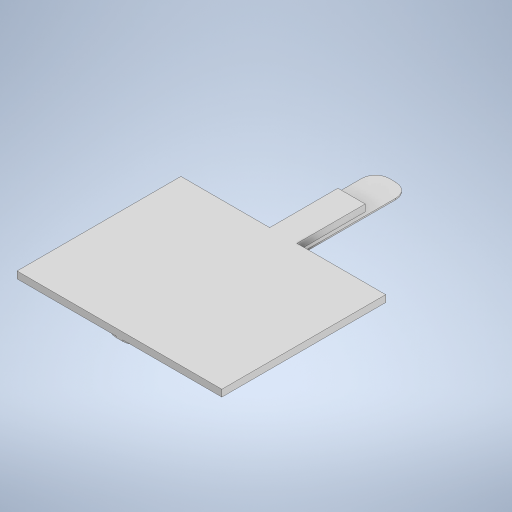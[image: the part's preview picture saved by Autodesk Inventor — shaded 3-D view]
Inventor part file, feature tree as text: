
AUTODESK INVENTOR PART (.ipt)
format: ipt  version: 2023 (Build 270158000, 158)  size: 243,200 bytes
history: native  units: in
note: dims shown in document units (in); Inventor stores cm internally (conversion verified against a paired STEP export)
features: extrude x2, sketch x2
ambient origin geometry x8: Origin, YZ Plane, XZ Plane, XY Plane, X Axis, Y Axis, Z Axis, Center Point
bodies: Solid1 (feature_tree)
feature tree (4):
  extrude  "Extrusion1"  Depth=4.7244in
  extrude  "Extrusion2"  Depth=1.9685in
  sketch  "Sketch1"  dims[d0=5.9055in d1=4.7244in]
  sketch  "Sketch2"  dims[d2=0.7874in d3=1.9685in d4=0.1969in d5=0.0in d6=0.9843in d7=7.874in d8=0.3937in d9=0.0394in d10=0.0in]
